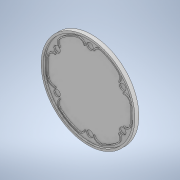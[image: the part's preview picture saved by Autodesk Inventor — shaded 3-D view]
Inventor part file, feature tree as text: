
AUTODESK INVENTOR PART (.ipt)
format: ipt  version: 2020 (Build 240168000, 168)  size: 251,392 bytes
history: native  units: in
note: dims shown in document units (in); Inventor stores cm internally (conversion verified against a paired STEP export)
features: extrude x4, sketch x4, projected_geometry x2
ambient origin geometry x8: Origin, YZ Plane, XZ Plane, XY Plane, X Axis, Y Axis, Z Axis, Center Point
bodies: Body1 (feature_tree)
feature tree (10):
  extrude  "Extrusion3"  Depth=5.1181in
  extrude  "Extrusion4"  Depth=0.1181in TaperAngle=0.0deg
  extrude  "Extrusion5"  Depth=2.2638in
  extrude  "Extrusion6"  Depth=0.06in TaperAngle=0.0deg
  sketch  "Sketch3"  dims[d27=5.3543in d28=5.1181in]
  sketch  "Sketch4"  dims[d29=5.5906in d30=0.1181in d31=0.0in]
  projected_geometry  "Projected Loop2"
  sketch  "Sketch5"  dims[d32=0.378in d33=2.2638in]
  projected_geometry  "Projected Loop3"
  sketch  "Sketch6"  dims[d34=2.3622in d36=360.0deg d38=0.06in d39=0.0in d40=0.0591in d41=2.3622in d43=360.0deg d45=5.1181in d46=0.7874in d47=0.7874in d48=2.3622in d50=360.0deg d52=0.0591in d53=0.0591in d54=2.3622in d56=360.0deg d58=0.0591in d59=0.0in d60=5.3543in d61=0.1181in d62=0.0in]
